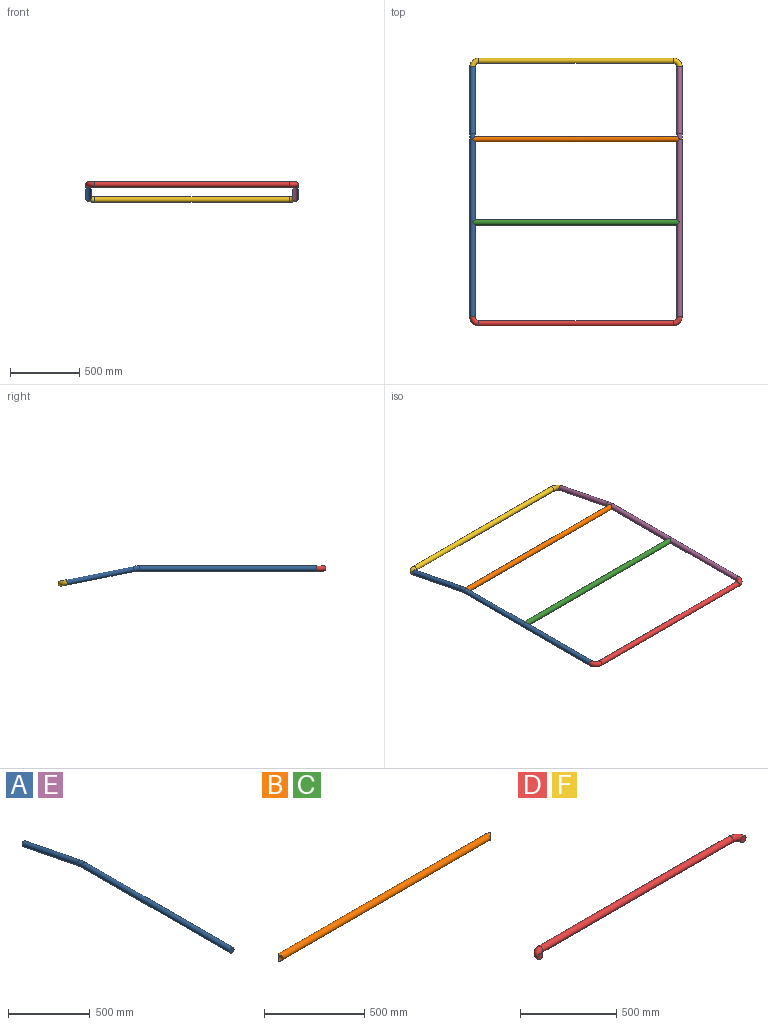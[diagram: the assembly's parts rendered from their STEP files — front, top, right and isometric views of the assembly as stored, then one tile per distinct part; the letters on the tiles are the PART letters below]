
ASSEMBLY  parts=6 mates=6
PART A: 5 faces, bbox 38x1803.7x138.7 mm
  f0: plane 38x37.26mm, normal (0,0.98,-0.2), area 1134.1mm2, adj f2
  f1: plane 38x38mm, normal (0,-1,0), area 1134.1mm2, adj f4
  f2: cylinder r=19mm len=488.03mm, axis (0,-0.98,0.2), area 58508.2mm2, adj f0,f3
  f3: torus R=200mm, axis (1,0,0), area 4713mm2, adj f2,f4
  f4: cylinder r=19mm len=1280.2mm, axis (0,-1,0), area 152830.5mm2, adj f1,f3
PART B: 3 faces, bbox 1492x38.1x38 mm
  f0: cylinder r=19mm len=1492mm, axis (1,0,0), area 175227.7mm2, adj f1,f2
  f1: cylinder r=19mm len=38.13mm, axis (0,1,0), area 1444mm2, adj f0
  f2: cylinder r=19mm len=38.13mm, axis (0,1,0), area 1444mm2, adj f0
PART C: same geometry as B
PART D: 5 faces, bbox 1540.7x70.4x38 mm
  f0: plane 38x38mm, normal (0,-1,0), area 1134.1mm2, adj f2
  f1: plane 38x38mm, normal (0,-1,0), area 1134.1mm2, adj f4
  f2: torus R=46mm, axis (0,0,-1), area 8626mm2, adj f0,f3
  f3: cylinder r=19mm len=1400mm, axis (1,0,0), area 167132.7mm2, adj f2,f4
  f4: torus R=46mm, axis (0,0,-1), area 8626mm2, adj f1,f3
PART E: same geometry as A
PART F: same geometry as D
PLACE A t=(-1448.08,-96.64,-40.06)mm fixed
PLACE B t=(-702.08,498.96,59.94)mm
PLACE C t=(-702.08,-101.14,59.94)mm
PLACE D rot(axis=(0,0,-1),180deg) t=(-702.08,-1011.47,59.94)mm
PLACE E t=(43.92,-96.64,-40.06)mm
PLACE F rot(axis=(-1,0,0),11.3deg) t=(-702.08,788.53,-40.06)mm
MATE fastened E.f4 <-> D.f0  axis (0,-1,0) through (43.92,-1011.47,59.94)mm
MATE fastened A.f4 <-> C.f2  axis (0,-1,0) through (-1448.08,-371.37,59.94)mm
MATE fastened D.f1 <-> A.f4  axis (0,1,0) through (-1448.08,-1011.47,59.94)mm
MATE fastened A.f2 <-> F.f0  axis (0,0.98,-0.2) through (-1448.08,788.53,-40.06)mm
MATE fastened F.f1 <-> E.f2  axis (0,-0.98,0.2) through (43.92,788.53,-40.06)mm
MATE fastened A.f4 <-> B.f2  axis (0,-1,0) through (-1448.08,268.73,59.94)mm
